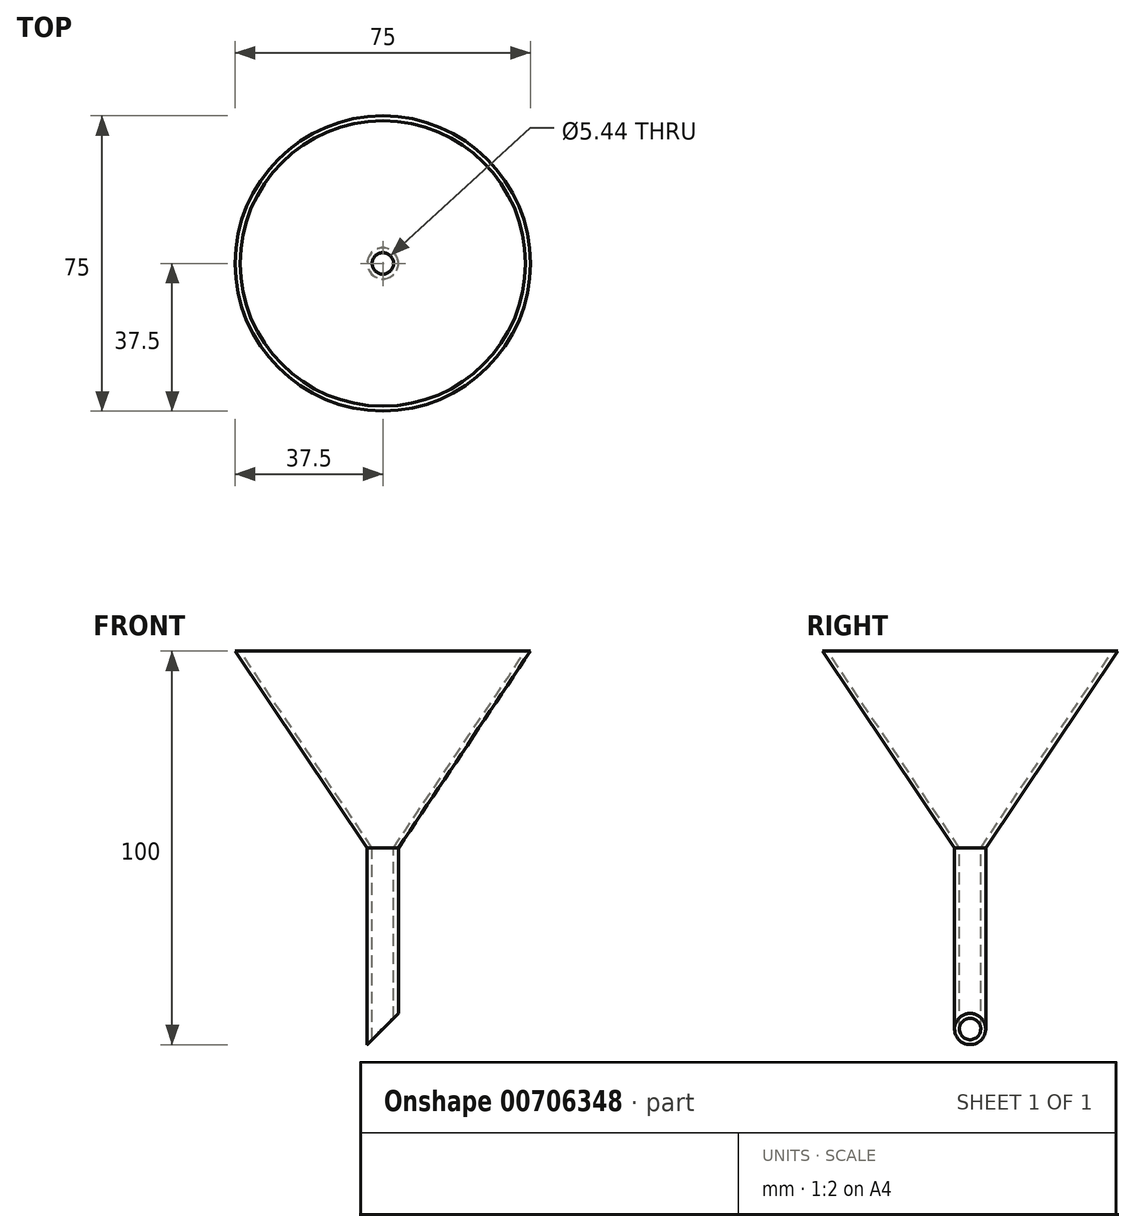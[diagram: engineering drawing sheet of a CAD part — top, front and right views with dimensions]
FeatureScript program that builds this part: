
annotation { "Feature Type Name" : "Feature", "Feature Type Description" : "" }
export const myFeature = defineFeature(function(context is Context, id is Id, definition is map)
    precondition{}
    {
        {
            var Q0;
            Q0=qCreatedBy(makeId("Top.planeOp"),FACE);
            var sketch = newSketch(context, id + "F0", { "sketchPlane" : qUnion([Q0])});
            skCircle(sketch, "E0", {"center": v(0, 0) * mm, "radius": 3.97 * mm});
            skSolve(sketch);
        }
        {
            var Q0;
            Q0=qCreatedBy(makeId("Top.planeOp"),FACE);
            cPlane(context, id + "F1", {"entities" : qUnion([Q0]), "cplaneType" : CPlaneType.OFFSET, "offset" : 50 * mm, "width" : 150 * mm, "height" : 150 * mm});
        }
        {
            var Q0;
            Q0=qCreatedBy(id+"F1.planeOp",FACE);
            var sketch = newSketch(context, id + "F2", { "sketchPlane" : qUnion([Q0])});
            skCircle(sketch, "E1", {"center": v(0, 0) * mm, "radius": 37.5 * mm});
            skSolve(sketch);
        }
        {
            var Q0;
            Q0=makeQuery(id+"F0.imprint","IMPRINT",FACE,{"disambiguationData":[TD([[makeQuery(id+"F0.imprint","IMPRINT",EDGE,{"derivedFrom":sQuery(id+"F0.wireOp",EDGE,"E0")}),1.0]])]});
            var Q1;
            Q1=makeQuery(id+"F2.imprint","IMPRINT",FACE,{"disambiguationData":[TD([[makeQuery(id+"F2.imprint","IMPRINT",EDGE,{"derivedFrom":sQuery(id+"F2.wireOp",EDGE,"E1")}),1.0]])]});
            loft(context, id + "F3", {"sheetProfilesArray" : [{ "sheetProfileEntities" : qUnion([Q0]) }, { "sheetProfileEntities" : qUnion([Q1]) }]});
        }
        {
            var Q0;
            Q0=qCreatedBy(id+"F1.planeOp",FACE);
            var sketch = newSketch(context, id + "F4", { "sketchPlane" : qUnion([Q0])});
            skCircle(sketch, "E2", {"center": v(0, 0) * mm, "radius": 36.25 * mm});
            skSolve(sketch);
        }
        {
            var Q0;
            Q0=qCreatedBy(makeId("Top.planeOp"),FACE);
            var sketch = newSketch(context, id + "F5", { "sketchPlane" : qUnion([Q0])});
            skCircle(sketch, "E3", {"center": v(0, 0) * mm, "radius": 2.72 * mm});
            skSolve(sketch);
        }
        {
            var Q1;
            Q1=makeQuery(id+"F5.imprint","IMPRINT",FACE,{"disambiguationData":[TD([[makeQuery(id+"F5.imprint","IMPRINT",EDGE,{"derivedFrom":sQuery(id+"F5.wireOp",EDGE,"E3")}),1.0]])]});
            var Q2;
            Q2=makeQuery(id+"F4.imprint","IMPRINT",FACE,{"disambiguationData":[TD([[makeQuery(id+"F4.imprint","IMPRINT",EDGE,{"derivedFrom":sQuery(id+"F4.wireOp",EDGE,"E2")}),1.0]])]});
            loft(context, id + "F6", {"operationType" : NewBodyOperationType.REMOVE, "sheetProfilesArray" : [{ "sheetProfileEntities" : qUnion([Q1]) }, { "sheetProfileEntities" : qUnion([Q2]) }]});
        }
        {
            var Q0;
            Q0=makeQuery(id+"F3.opLoft","CAP_FACE",FACE,{"disambiguationData":[OSD([makeQuery(id+"F0.imprint","IMPRINT",FACE,{"disambiguationData":[TD([[makeQuery(id+"F0.imprint","IMPRINT",EDGE,{"derivedFrom":sQuery(id+"F0.wireOp",EDGE,"E0")}),1.0]])]})])],"isStart":true});
            extrude(context, id + "F7", {"entities" : qUnion([Q0]), "operationType" : NewBodyOperationType.ADD, "depth" : 50 * mm, "offsetDistance" : 25 * mm});
        }
        {
            var Q0;
            Q0=qCreatedBy(makeId("Front.planeOp"),FACE);
            var sketch = newSketch(context, id + "F8", { "sketchPlane" : qUnion([Q0])});
            skLineSegment(sketch, "E4", {"start": v(3.97, -42.06) * mm, "end": v(-3.97, -50) * mm});
            skSolve(sketch);
        }
        {
            var Q0;
            Q0=qCreatedBy(makeId("Right.planeOp"),FACE);
            var sketch = newSketch(context, id + "F9", { "sketchPlane" : qUnion([Q0])});
            skLineSegment(sketch, "E5.bottom", {"start": v(3.97, -53.97) * mm, "end": v(-3.97, -53.97) * mm});
            skLineSegment(sketch, "E5.top", {"start": v(3.97, -46.03) * mm, "end": v(-3.97, -46.03) * mm});
            skLineSegment(sketch, "E5.left", {"start": v(3.97, -53.97) * mm, "end": v(3.97, -46.03) * mm});
            skLineSegment(sketch, "E5.right", {"start": v(-3.97, -53.97) * mm, "end": v(-3.97, -46.03) * mm});
            skSolve(sketch);
        }
        {
            var Q0;
            Q0=makeQuery(id+"F9.imprint","IMPRINT",FACE,{"disambiguationData":[TD([[makeQuery(id+"F9.imprint","IMPRINT",EDGE,{"derivedFrom":sQuery(id+"F9.wireOp",EDGE,"E5.bottom")}),-1.0]])]});
            var Q1;
            Q1=sQuery(id+"F8.wireOp",EDGE,"E4");
            sweep(context, id + "F10", {"operationType" : NewBodyOperationType.REMOVE, "profiles" : qUnion([Q0]), "path" : qUnion([Q1])});
        }
    });
